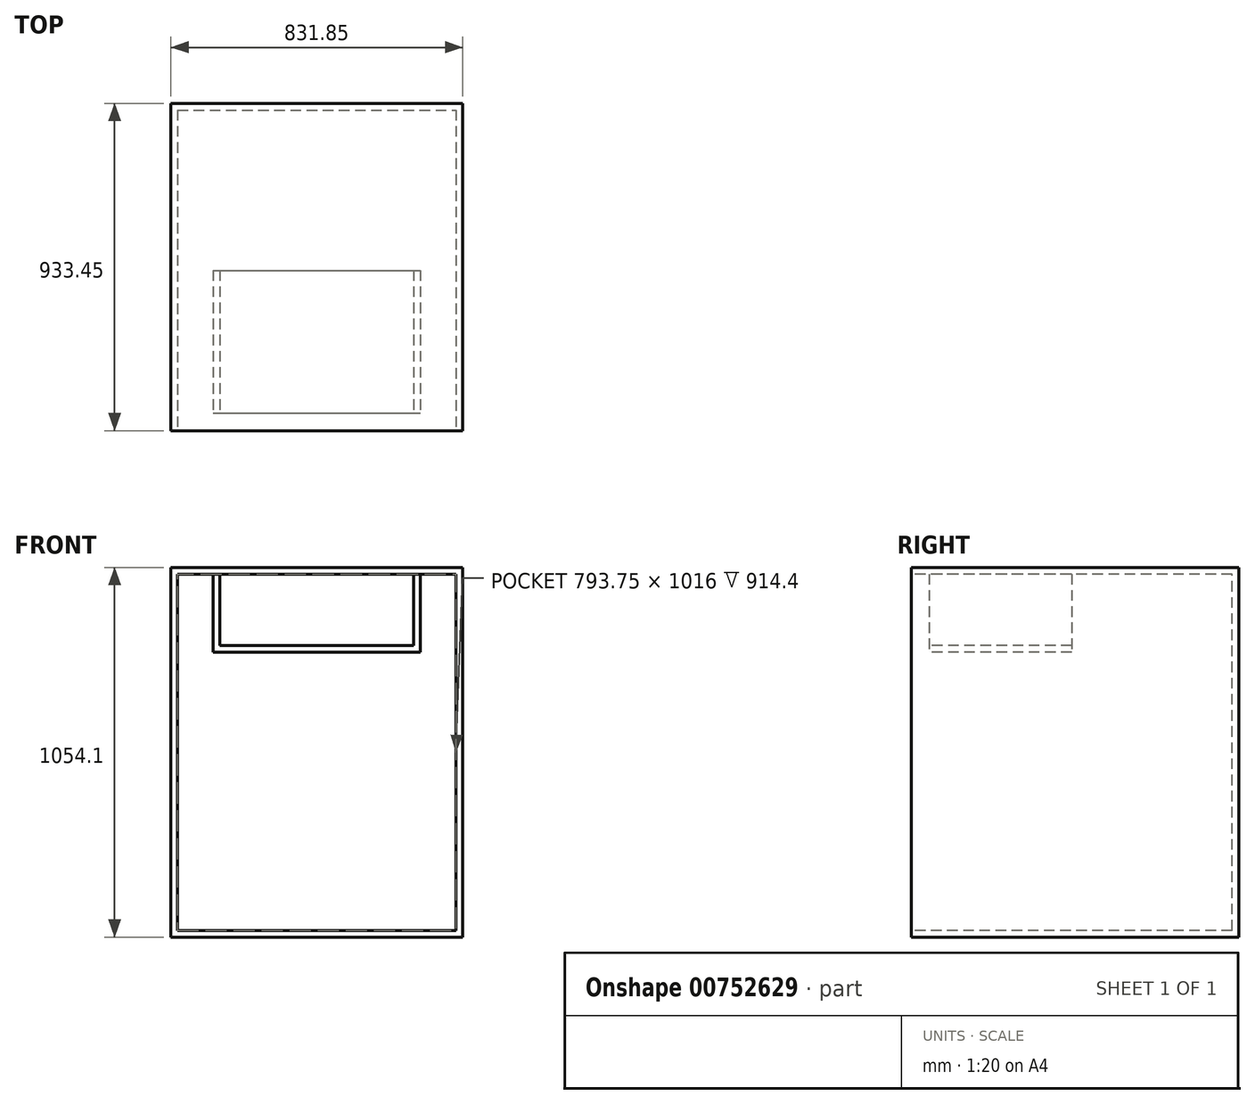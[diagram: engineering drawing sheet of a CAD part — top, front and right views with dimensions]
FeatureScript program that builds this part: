
annotation { "Feature Type Name" : "Feature", "Feature Type Description" : "" }
export const myFeature = defineFeature(function(context is Context, id is Id, definition is map)
    precondition{}
    {
        {
            var Q0;
            Q0=qCreatedBy(makeId("Front.planeOp"),FACE);
            var sketch = newSketch(context, id + "F0", { "sketchPlane" : qUnion([Q0])});
            skLineSegment(sketch, "E0.bottom", {"start": v(0, 0) * mm, "end": v(793.75, 0) * mm});
            skLineSegment(sketch, "E0.top", {"start": v(0, 1016) * mm, "end": v(793.75, 1016) * mm});
            skLineSegment(sketch, "E0.left", {"start": v(0, 0) * mm, "end": v(0, 1016) * mm});
            skLineSegment(sketch, "E0.right", {"start": v(793.75, 0) * mm, "end": v(793.75, 1016) * mm});
            skLineSegment(sketch, "E1.0", {"start": v(-19.05, 1035.05) * mm, "end": v(812.8, 1035.05) * mm});
            skLineSegment(sketch, "E1.1", {"start": v(-19.05, -19.05) * mm, "end": v(-19.05, 1035.05) * mm});
            skLineSegment(sketch, "E1.2", {"start": v(-19.05, -19.05) * mm, "end": v(812.8, -19.05) * mm});
            skLineSegment(sketch, "E1.3", {"start": v(812.8, -19.05) * mm, "end": v(812.8, 1035.05) * mm});
            skSolve(sketch);
        }
        {
            var Q0;
            Q0=makeQuery(id+"F0.imprint","IMPRINT",FACE,{"disambiguationData":[TD([[makeQuery(id+"F0.imprint","IMPRINT",EDGE,{"derivedFrom":sQuery(id+"F0.wireOp",EDGE,"E0.bottom")}),-1.0]])]});
            extrude(context, id + "F1", {"entities" : qUnion([Q0]), "oppositeDirection" : true, "depth" : 914.4 * mm, "offsetDistance" : 25.4 * mm});
        }
        {
            var Q0;
            Q0=makeQuery(id+"F1.opExtrude","CAP_FACE",FACE,{"disambiguationData":[OSD([sQuery(id+"F0.wireOp",EDGE,"E0.bottom"),sQuery(id+"F0.wireOp",EDGE,"E0.top"),sQuery(id+"F0.wireOp",EDGE,"E0.left"),sQuery(id+"F0.wireOp",EDGE,"E0.right"),sQuery(id+"F0.wireOp",EDGE,"E1.0"),sQuery(id+"F0.wireOp",EDGE,"E1.1"),sQuery(id+"F0.wireOp",EDGE,"E1.2"),sQuery(id+"F0.wireOp",EDGE,"E1.3")])],"isStart":false});
            var sketch = newSketch(context, id + "F2", { "sketchPlane" : qUnion([Q0])});
            skLineSegment(sketch, "E2.0", {"start": v(19.05, 1035.05) * mm, "end": v(-812.8, 1035.05) * mm});
            skLineSegment(sketch, "E3.0", {"start": v(-812.8, -19.05) * mm, "end": v(-812.8, 1035.05) * mm});
            skLineSegment(sketch, "E4.0", {"start": v(19.05, -19.05) * mm, "end": v(19.05, 1035.05) * mm});
            skLineSegment(sketch, "E5.0", {"start": v(19.05, -19.05) * mm, "end": v(-812.8, -19.05) * mm});
            skSolve(sketch);
        }
        {
            var Q0;
            Q0 = qSketchRegion(id + "F2", true);
            extrude(context, id + "F3", {"entities" : qUnion([Q0]), "operationType" : NewBodyOperationType.ADD, "depth" : 19.05 * mm, "offsetDistance" : 25.4 * mm});
        }
        {
            var Q0;
            Q0=qCreatedBy(makeId("Front.planeOp"),FACE);
            cPlane(context, id + "F4", {"entities" : qUnion([Q0]), "cplaneType" : CPlaneType.OFFSET, "offset" : 50.8 * mm, "oppositeDirection" : true, "width" : 152.4 * mm, "height" : 152.4 * mm});
        }
        {
            var Q0;
            Q0=qCreatedBy(id+"F4.planeOp",FACE);
            var sketch = newSketch(context, id + "F5", { "sketchPlane" : qUnion([Q0])});
            skLineSegment(sketch, "E6.0", {"start": v(0, 1016) * mm, "end": v(793.75, 1016) * mm});
            skLineSegment(sketch, "E7.bottom", {"start": v(120.65, 1016) * mm, "end": v(673.1, 1016) * mm});
            skLineSegment(sketch, "E7.top", {"start": v(120.65, 812.8) * mm, "end": v(673.1, 812.8) * mm});
            skLineSegment(sketch, "E7.left", {"start": v(120.65, 1016) * mm, "end": v(120.65, 812.8) * mm});
            skLineSegment(sketch, "E7.right", {"start": v(673.1, 1016) * mm, "end": v(673.1, 812.8) * mm});
            skLineSegment(sketch, "E8.0", {"start": v(692.15, 1016) * mm, "end": v(692.15, 793.75) * mm});
            skLineSegment(sketch, "E8.1", {"start": v(101.6, 793.75) * mm, "end": v(692.15, 793.75) * mm});
            skLineSegment(sketch, "E8.2", {"start": v(101.6, 1016) * mm, "end": v(101.6, 793.75) * mm});
            skSolve(sketch);
        }
        {
            var Q0;
            Q0=makeQuery(id+"F5.imprint","IMPRINT",FACE,{"disambiguationData":[TD([[makeQuery(id+"F5.imprint","IMPRINT",EDGE,{"derivedFrom":sQuery(id+"F5.wireOp",EDGE,"E7.top")}),-1.0]])]});
            extrude(context, id + "F6", {"entities" : qUnion([Q0]), "operationType" : NewBodyOperationType.ADD, "oppositeDirection" : true, "depth" : 406.4 * mm, "offsetDistance" : 25.4 * mm});
        }
    });
